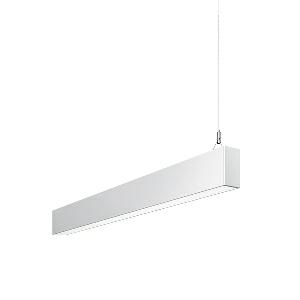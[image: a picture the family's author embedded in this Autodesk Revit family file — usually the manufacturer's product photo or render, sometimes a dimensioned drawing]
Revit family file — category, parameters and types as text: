
# Revit family: idoo_line_-_ilp_4000_830_d_end_00805738_457d
name_source: partatom
category: Lighting Fixtures
units: mm (PartAtom-declared; Revit-internal decimal feet)

## family parameters
Cut with Voids When Loaded = No
Host = Face
Light Source = No
Part Type = Normal
Room Calculation Point = No
Round Connector Dimension = Use Diameter
Shared = No

## types (1)
- IDOO.line - ILP 4000/830/D END (1 x LED, 3750 lm, 3000K)
    Apparent Load = 29 VA
    Approval mark = CE
    CIE Flux Codes = 66 91 98 40 100
    Color Rendering = 80-89
    Color Temperature = 3000K
    Control Gear = Electronic ballast
    Default Elevation = 1800 mm
    Description = ILP 4000/830/D|Suspended luminaire|light source: LED|connected load: 220-240 V, 50/60 Hz|Power consumption: approx. 29 W|standby: approx. 0,15|luminous flux: 3750 lm|luminous efficacy: 129 lm/W|light distribution: Direct/indirect|direct ratio: approx. 40 %|colour temperature: Warm white, ca. 3000 K|color rendering index (CRI): >= 80|chromaticity tolerance:  3 SDCM|System of protection: IP 40|technology: Continuously dimmable|luminaire body|material: Sectional aluminium|colour: White|lamp cover: Acrylic (PMMA), Clear|mains lead: 1,0 m With free stranded wires|Fastening: Steel cable 0.3 - 0.7 m|glare control: Prism aperture|luminance(L65): <= 2700 cd/m|unified glare rating(4H 8H): <=  16|special features: DALI Load 1x, TouchDIM - dimming via standard switch, Through-wired, up to 18 m on one mains connection, Flicker-free, Suitable as emergency lighting, Mechanical and electrical connection of the individual modules without tools|
    Frequency = 50 Hz
    Height = 110 mm
    Lamp = 1 x LED
    Lamp Light Flux = 3750 lm
    Lamp count = 1
    Length = 1408 mm
    Luminous efficacy = 129 lm/W
    Manufacturer = Waldmann
    ModVariant = No
    Model = 00805738
    Mounting Place = Ceiling
    Mounting Type = Pendant
    Number of Poles = 1
    OnlyDefault = Yes
    Power Factor = 1
    Product Name = IDOO.line - ILP 4000/830/D END
    Product group = Suspended luminaire
    ProductGroupID = 9
    Protection Class = Protection class I
    Protection Degree = IP 40
    RLX_Detail_Level = 1
    RLX_Emergency_Light_Flux = 0 lm
    RLX_Emergency_Type = 0
    RLX_Emergency_Type_DB = No
    RlxData = <blob elided: 18621 chars, md5=74cc859d>
    Socket = socket
    Standby Power = 0 W
    System Light Flux = 3750 lm
    System Power = 29 W
    Type Comments = Product without accessories
    Type Image = 113309000-00692591.jpg
    URL = http://relux.com
    VarID = ---
    Voltage = 230 V
    Voltage Range = 220-240 V
    Weight = 0.00 kg
    Width = 60 mm  [stored 0.19685 ft]

note: [stored X ft] marks values corroborated as IEEE doubles in the binary element streams (Revit-internal decimal feet)

## geometry (parser evidence)
native form markers: Blend x4, Sweep x15
no freeform markers — native parametric forms only
